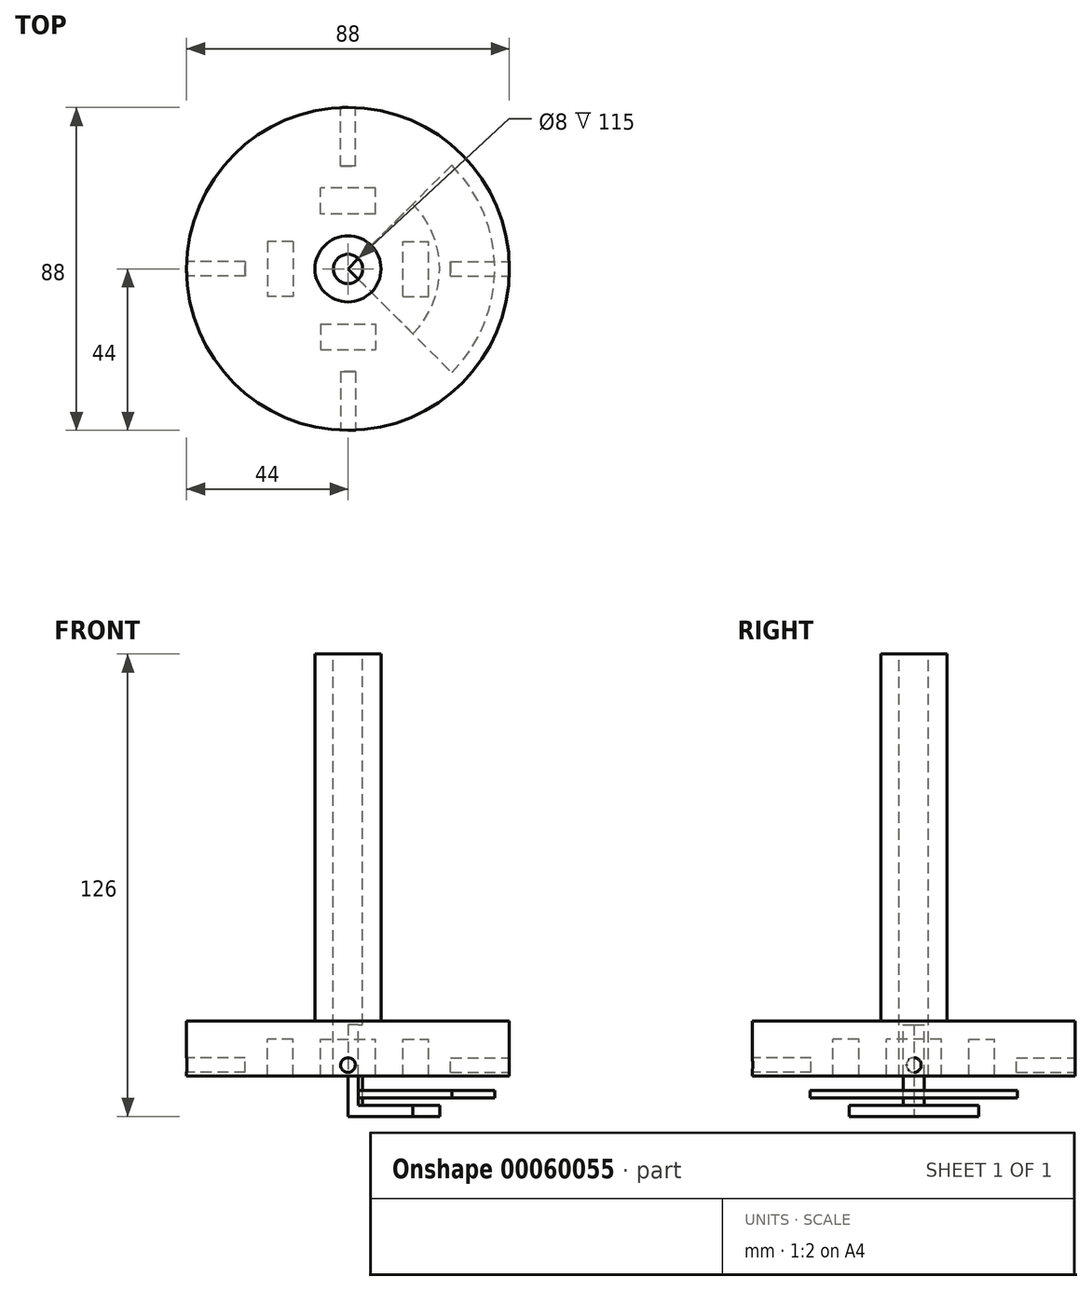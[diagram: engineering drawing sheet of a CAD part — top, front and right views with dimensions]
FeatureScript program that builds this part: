
annotation { "Feature Type Name" : "Feature", "Feature Type Description" : "" }
export const myFeature = defineFeature(function(context is Context, id is Id, definition is map)
    precondition{}
    {
        {
            var Q0;
            Q0=qCreatedBy(makeId("Front.planeOp"),FACE);
            var sketch = newSketch(context, id + "F0", { "sketchPlane" : qUnion([Q0])});
            skLineSegment(sketch, "E0", {"start": v(0, 0) * mm, "end": v(0, 123.18) * mm, "construction": true});
            skLineSegment(sketch, "E1", {"start": v(0, 0) * mm, "end": v(131.26, 0) * mm, "construction": true});
            skLineSegment(sketch, "E2", {"start": v(0, 0) * mm, "end": v(25, 0) * mm});
            skLineSegment(sketch, "E3", {"start": v(25, 0) * mm, "end": v(25, 3) * mm});
            skLineSegment(sketch, "E4", {"start": v(25, 3) * mm, "end": v(4, 3) * mm});
            skLineSegment(sketch, "E5", {"start": v(4, 3) * mm, "end": v(4, 25) * mm});
            skLineSegment(sketch, "E6", {"start": v(4, 25) * mm, "end": v(0, 25) * mm});
            skLineSegment(sketch, "E7", {"start": v(0, 25) * mm, "end": v(0, 0) * mm});
            skSolve(sketch);
        }
        {
            var Q0;
            Q0 = qSketchRegion(id + "F0", true);
            var Q1;
            Q1=sQuery(id+"F0.wireOp",EDGE,"E7");
            revolve(context, id + "F1", {"entities" : qUnion([Q0]), "axis" : qUnion([Q1]), "revolveType" : RevolveType.FULL});
        }
        {
            var Q0;
            Q0=qCreatedBy(makeId("Front.planeOp"),FACE);
            var sketch = newSketch(context, id + "F2", { "sketchPlane" : qUnion([Q0])});
            skLineSegment(sketch, "E8", {"start": v(4, 5) * mm, "end": v(40, 5) * mm});
            skLineSegment(sketch, "E9", {"start": v(40, 5) * mm, "end": v(40, 7) * mm});
            skLineSegment(sketch, "E10", {"start": v(40, 7) * mm, "end": v(4, 7) * mm});
            skLineSegment(sketch, "E11", {"start": v(4, 7) * mm, "end": v(4, 5) * mm});
            skSolve(sketch);
        }
        {
            var Q0;
            Q0 = qSketchRegion(id + "F2", true);
            var Q1;
            Q1=sQuery(id+"F0.wireOp",EDGE,"E7");
            revolve(context, id + "F3", {"entities" : qUnion([Q0]), "axis" : qUnion([Q1]), "revolveType" : RevolveType.FULL});
        }
        {
            var Q0;
            Q0=qCreatedBy(makeId("Front.planeOp"),FACE);
            var sketch = newSketch(context, id + "F4", { "sketchPlane" : qUnion([Q0])});
            skLineSegment(sketch, "E12", {"start": v(4, 126) * mm, "end": v(4, 11) * mm});
            skLineSegment(sketch, "E13", {"start": v(4, 11) * mm, "end": v(44, 11) * mm});
            skLineSegment(sketch, "E14", {"start": v(44, 11) * mm, "end": v(44, 26) * mm});
            skLineSegment(sketch, "E15", {"start": v(44, 26) * mm, "end": v(9, 26) * mm});
            skLineSegment(sketch, "E16", {"start": v(9, 26) * mm, "end": v(9, 126) * mm});
            skLineSegment(sketch, "E17", {"start": v(9, 126) * mm, "end": v(4, 126) * mm});
            skSolve(sketch);
        }
        {
            var Q0;
            Q0 = qSketchRegion(id + "F4", true);
            var Q1;
            Q1=sQuery(id+"F0.wireOp",EDGE,"E7");
            revolve(context, id + "F5", {"entities" : qUnion([Q0]), "axis" : qUnion([Q1]), "revolveType" : RevolveType.FULL});
        }
        {
            var Q0;
            Q0=qCreatedBy(makeId("Front.planeOp"),FACE);
            var sketch = newSketch(context, id + "F6", { "sketchPlane" : qUnion([Q0])});
            skLineSegment(sketch, "E18", {"start": v(0, 11) * mm, "end": v(44, 11) * mm, "construction": true});
            skSolve(sketch);
        }
        {
            var Q0;
            Q0=sQuery(id+"F6.wireOp",VERTEX,"E18.end");
            var Q1;
            Q1=sQuery(id+"F6.wireOp",EDGE,"E18");
            cPlane(context, id + "F7", {"entities" : qUnion([Q0, Q1]), "cplaneType" : CPlaneType.LINE_POINT, "offset" : 150 * mm, "width" : 150 * mm, "height" : 150 * mm});
        }
        {
            var Q0;
            Q0=qCreatedBy(id+"F7.planeOp",FACE);
            var sketch = newSketch(context, id + "F8", { "sketchPlane" : qUnion([Q0])});
            skCircle(sketch, "E19", {"center": v(0, 14) * mm, "radius": 2 * mm});
            skSolve(sketch);
        }
        {
            var Q0;
            Q0 = qSketchRegion(id + "F8", true);
            extrude(context, id + "F9", {"entities" : qUnion([Q0]), "operationType" : NewBodyOperationType.REMOVE, "oppositeDirection" : true, "depth" : 16 * mm});
        }
        {
            var Q0;
            Q0=qCreatedBy(makeId("Front.planeOp"),FACE);
            var sketch = newSketch(context, id + "F10", { "sketchPlane" : qUnion([Q0])});
            skLineSegment(sketch, "E20.bottom", {"start": v(16, 20) * mm, "end": v(21, 20) * mm, "construction": true});
            skLineSegment(sketch, "E20.top", {"start": v(16, 7) * mm, "end": v(21, 7) * mm});
            skLineSegment(sketch, "E20.left", {"start": v(16, 20) * mm, "end": v(16, 7) * mm, "construction": true});
            skLineSegment(sketch, "E20.right", {"start": v(21, 20) * mm, "end": v(21, 7) * mm, "construction": true});
            skLineSegment(sketch, "E21.bottom", {"start": v(15, 7) * mm, "end": v(22, 7) * mm});
            skLineSegment(sketch, "E21.top", {"start": v(15, 21) * mm, "end": v(22, 21) * mm});
            skLineSegment(sketch, "E21.left", {"start": v(15, 7) * mm, "end": v(15, 21) * mm});
            skLineSegment(sketch, "E21.right", {"start": v(22, 7) * mm, "end": v(22, 21) * mm});
            skSolve(sketch);
        }
        {
            var Q0;
            Q0 = qSketchRegion(id + "F10", true);
            extrude(context, id + "F11", {"entities" : qUnion([Q0]), "operationType" : NewBodyOperationType.REMOVE, "endBound" : BoundingType.SYMMETRIC, "oppositeDirection" : true, "depth" : 15 * mm});
        }
        {
            var Q0;
            Q0=qCreatedBy(makeId("Top.planeOp"),FACE);
            var sketch = newSketch(context, id + "F12", { "sketchPlane" : qUnion([Q0])});
            skLineSegment(sketch, "E22", {"start": v(0, 0) * mm, "end": v(61.62, 61.62) * mm});
            skLineSegment(sketch, "E23", {"start": v(61.62, 61.62) * mm, "end": v(61.62, -61.62) * mm, "construction": true});
            skLineSegment(sketch, "E24", {"start": v(61.62, -61.62) * mm, "end": v(0, 0) * mm});
            skLineSegment(sketch, "E25", {"start": v(0, 0) * mm, "end": v(61.62, 0) * mm});
            skLineSegment(sketch, "E26", {"start": v(61.62, 61.62) * mm, "end": v(-57.42, 61.62) * mm});
            skLineSegment(sketch, "E27", {"start": v(-57.42, 61.62) * mm, "end": v(-60.96, -39.96) * mm});
            skLineSegment(sketch, "E28", {"start": v(-60.96, -39.96) * mm, "end": v(61.62, -61.62) * mm});
            skSolve(sketch);
        }
        {
            var Q0;
            Q0 = qSketchRegion(id + "F12", true);
            extrude(context, id + "F13", {"entities" : qUnion([Q0]), "operationType" : NewBodyOperationType.REMOVE, "endBound" : BoundingType.THROUGH_ALL, "depth" : 25 * mm});
        }
        {
            var Q0;
            Q0=makeQuery(id+"F5.opRevolve","SWEPT_BODY",BODY,{"disambiguationData":[OSD([sQuery(id+"F4.wireOp",EDGE,"E12"),sQuery(id+"F4.wireOp",EDGE,"E13"),sQuery(id+"F4.wireOp",EDGE,"E14"),sQuery(id+"F4.wireOp",EDGE,"E15"),sQuery(id+"F4.wireOp",EDGE,"E16"),sQuery(id+"F4.wireOp",EDGE,"E17")])]});
            var Q1;
            Q1=sQuery(id+"F0.wireOp",EDGE,"E0");
            circularPattern(context, id + "F14", {"operationType" : NewBodyOperationType.ADD, "entities" : qUnion([Q0]), "axis" : qUnion([Q1]), "angle" : 360 * degree, "instanceCount" : 4, "equalSpace" : true});
        }
    });
